# Revit family: Indoor_Pendant Lamp_Santa&Cole_Cirio Circular
name_source: partatom
category: Luminarias
revit_build: Autodesk Revit 2018 (Build: 20190510_1515(x64)
units: mm (PartAtom-declared; Revit-internal decimal feet)

## family parameters
Anfitrión = Cara
Compartido = No
Corte con vacíos al cargar = No
Cota de conector redondo = Diámetro de uso
Origen de luz = No
Punto de cálculo de habitación = No
Tipo de pieza = Normal

## types (4) — shared parameters
Assembly Instructions - CE = https://www.santacole.com
Assembly Instructions - UL = https://www.santacole.com
Elevación por defecto = 1219 mm
Energy Label = https://www.santacole.com
Fabricante = Santa & Cole
Lampshade Material = Santa&Cole - White Matte Finish
Manufacturer website = http://www.santacole.com
Technical Information = https://www.santacole.com
URL = https://www.santacole.com

## per-type parameters (varying)
| type | Carga aparente | Cirio Circular L | Cirio Circular M | Cirio Circular S | Cirio Oval | Code | Load | Modelo |
| Cirio Circular S | 92 W | No | No | Sí | No | CIR12+CIFxx+CIPxx | 92 W | Cirio Circular |
| Cirio Circular M | 216 W | No | Sí | No | No | CIR28+CIFxx+CIPxx | 216 W | Cirio Circular |
| Cirio Circular L | 323 W | Sí | No | No | No | CIR42+CIFxx+CIPxx | 323 W | Cirio Circular |
| Cirio Oval | 293 W | No | No | No | Sí | CIL05+CII05+CIR28+CIFxx+CIPxx+CIN01 | 293 W | Cirio Oval |

## geometry (parser evidence)
native form markers: Blend x4, Sweep x5
no freeform markers — native parametric forms only
